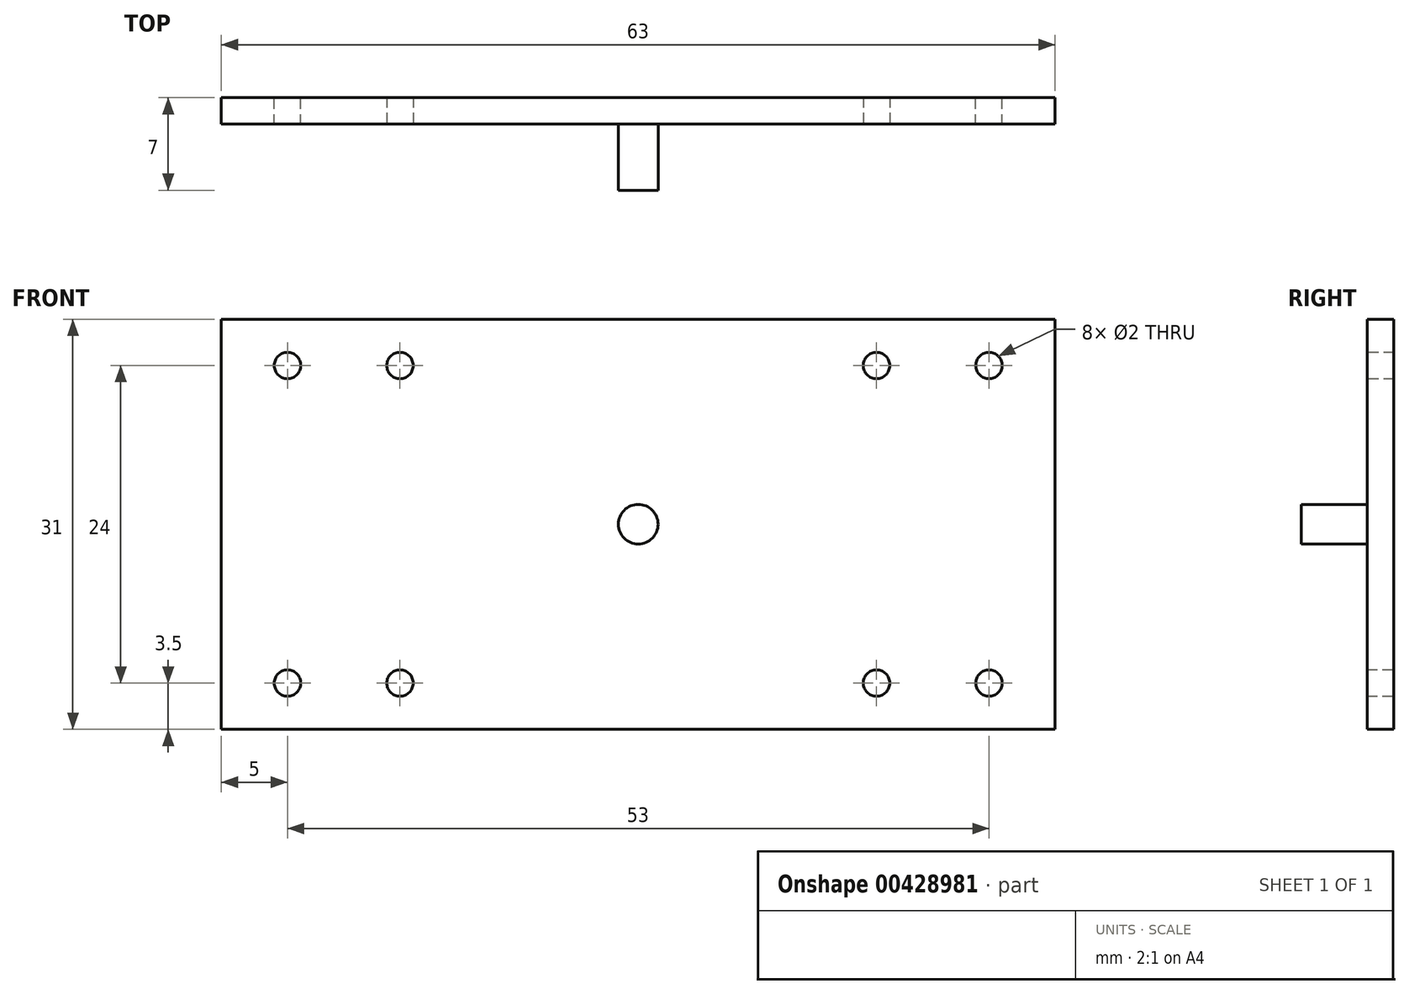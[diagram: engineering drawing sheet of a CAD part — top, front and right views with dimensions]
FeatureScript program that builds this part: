
annotation { "Feature Type Name" : "Feature", "Feature Type Description" : "" }
export const myFeature = defineFeature(function(context is Context, id is Id, definition is map)
    precondition{}
    {
        {
            var Q0;
            Q0=qCreatedBy(makeId("Front.planeOp"),FACE);
            var sketch = newSketch(context, id + "F0", { "sketchPlane" : qUnion([Q0])});
            skLineSegment(sketch, "E0.bottom", {"start": v(21.5, 15.5) * mm, "end": v(-21.5, 15.5) * mm});
            skLineSegment(sketch, "E0.top", {"start": v(21.5, -15.5) * mm, "end": v(-21.5, -15.5) * mm});
            skLineSegment(sketch, "E0.left", {"start": v(21.5, 15.5) * mm, "end": v(21.5, -15.5) * mm});
            skLineSegment(sketch, "E0.right", {"start": v(-21.5, 15.5) * mm, "end": v(-21.5, -15.5) * mm});
            skPoint(sketch, "E0.middle", {"position": v(0, 0) * mm});
            skSolve(sketch);
        }
        {
            var Q0;
            Q0 = qSketchRegion(id + "F0", true);
            extrude(context, id + "F1", {"entities" : qUnion([Q0]), "depth" : 2 * mm});
        }
        {
            var Q0;
            Q0=makeQuery(id+"F1.opExtrude","CAP_FACE",FACE,{"disambiguationData":[OSD([sQuery(id+"F0.wireOp",EDGE,"E0.bottom"),sQuery(id+"F0.wireOp",EDGE,"E0.top"),sQuery(id+"F0.wireOp",EDGE,"E0.left"),sQuery(id+"F0.wireOp",EDGE,"E0.right")])],"isStart":false});
            var sketch = newSketch(context, id + "F2", { "sketchPlane" : qUnion([Q0])});
            skCircle(sketch, "E1", {"center": v(0, 0) * mm, "radius": 1.5 * mm});
            skSolve(sketch);
        }
        {
            var Q0;
            Q0 = qSketchRegion(id + "F2", true);
            extrude(context, id + "F3", {"entities" : qUnion([Q0]), "operationType" : NewBodyOperationType.ADD, "depth" : 5 * mm});
        }
        {
            var Q0;
            Q0=makeQuery(id+"F1.opExtrude","CAP_FACE",FACE,{"disambiguationData":[OSD([sQuery(id+"F0.wireOp",EDGE,"E0.bottom"),sQuery(id+"F0.wireOp",EDGE,"E0.top"),sQuery(id+"F0.wireOp",EDGE,"E0.left"),sQuery(id+"F0.wireOp",EDGE,"E0.right")])],"isStart":false});
            var sketch = newSketch(context, id + "F4", { "sketchPlane" : qUnion([Q0])});
            skLineSegment(sketch, "E2.bottom", {"start": v(21.5, 15.5) * mm, "end": v(14.5, 15.5) * mm, "construction": true});
            skLineSegment(sketch, "E2.top", {"start": v(21.5, 8.5) * mm, "end": v(14.5, 8.5) * mm, "construction": true});
            skLineSegment(sketch, "E2.left", {"start": v(21.5, 15.5) * mm, "end": v(21.5, 8.5) * mm, "construction": true});
            skLineSegment(sketch, "E2.right", {"start": v(14.5, 15.5) * mm, "end": v(14.5, 8.5) * mm, "construction": true});
            skLineSegment(sketch, "E3", {"start": v(14.5, 8.5) * mm, "end": v(21.5, 15.5) * mm, "construction": true});
            skCircle(sketch, "E4", {"center": v(18, 12) * mm, "radius": 1 * mm});
            skCircle(sketch, "E5.MirrorC", {"center": v(18, -12) * mm, "radius": 1 * mm});
            skCircle(sketch, "E6.MirrorC", {"center": v(-18, 12) * mm, "radius": 1 * mm});
            skCircle(sketch, "E7.MirrorC", {"center": v(-18, -12) * mm, "radius": 1 * mm});
            skSolve(sketch);
        }
        {
            var Q0;
            Q0 = qSketchRegion(id + "F4", true);
            extrude(context, id + "F5", {"entities" : qUnion([Q0]), "operationType" : NewBodyOperationType.REMOVE, "endBound" : BoundingType.THROUGH_ALL, "oppositeDirection" : true, "depth" : 25 * mm});
        }
        {
            var Q0;
            Q0=qCreatedBy(makeId("Front.planeOp"),FACE);
            var sketch = newSketch(context, id + "F6", { "sketchPlane" : qUnion([Q0])});
            skLineSegment(sketch, "E8.0.0", {"start": v(-21.5, -15.5) * mm, "end": v(21.5, -15.5) * mm});
            skLineSegment(sketch, "E8.0.1", {"start": v(21.5, -15.5) * mm, "end": v(21.5, 15.5) * mm});
            skLineSegment(sketch, "E8.0.2", {"start": v(21.5, 15.5) * mm, "end": v(-21.5, 15.5) * mm});
            skLineSegment(sketch, "E8.0.3", {"start": v(-21.5, 15.5) * mm, "end": v(-21.5, -15.5) * mm});
            skLineSegment(sketch, "E9.bottom", {"start": v(21.5, 15.5) * mm, "end": v(31.5, 15.5) * mm});
            skLineSegment(sketch, "E9.top", {"start": v(21.5, -15.5) * mm, "end": v(31.5, -15.5) * mm});
            skLineSegment(sketch, "E9.left", {"start": v(21.5, 15.5) * mm, "end": v(21.5, -15.5) * mm});
            skLineSegment(sketch, "E9.right", {"start": v(31.5, 15.5) * mm, "end": v(31.5, -15.5) * mm});
            skPoint(sketch, "E10.oppositeSnap0", {"position": v(26.5, -15.5) * mm});
            skLineSegment(sketch, "E10.bottom", {"start": v(-21.5, 15.5) * mm, "end": v(-31.5, 15.5) * mm});
            skLineSegment(sketch, "E10.top", {"start": v(-21.5, -15.5) * mm, "end": v(-31.5, -15.5) * mm});
            skLineSegment(sketch, "E10.right", {"start": v(-31.5, 15.5) * mm, "end": v(-31.5, -15.5) * mm});
            skCircle(sketch, "E11.0", {"center": v(18, 12) * mm, "radius": 1 * mm});
            skCircle(sketch, "E12", {"center": v(26.5, 12) * mm, "radius": 1 * mm});
            skPoint(sketch, "E12.centerSnap0", {"position": v(26.5, 15.5) * mm});
            skCircle(sketch, "E13.MirrorC", {"center": v(26.5, -12) * mm, "radius": 1 * mm});
            skCircle(sketch, "E14.MirrorC", {"center": v(-26.5, 12) * mm, "radius": 1 * mm});
            skCircle(sketch, "E15.MirrorC", {"center": v(-26.5, -12) * mm, "radius": 1 * mm});
            skSolve(sketch);
        }
        {
            var Q0;
            Q0 = qSketchRegion(id + "F6", true);
            extrude(context, id + "F7", {"entities" : qUnion([Q0]), "operationType" : NewBodyOperationType.ADD, "depth" : 2 * mm});
        }
        {
            var Q0;
            Q0 = qSketchRegion(id + "F4", true);
            extrude(context, id + "F8", {"entities" : qUnion([Q0]), "operationType" : NewBodyOperationType.REMOVE, "endBound" : BoundingType.THROUGH_ALL, "oppositeDirection" : true, "depth" : 25 * mm});
        }
    });
